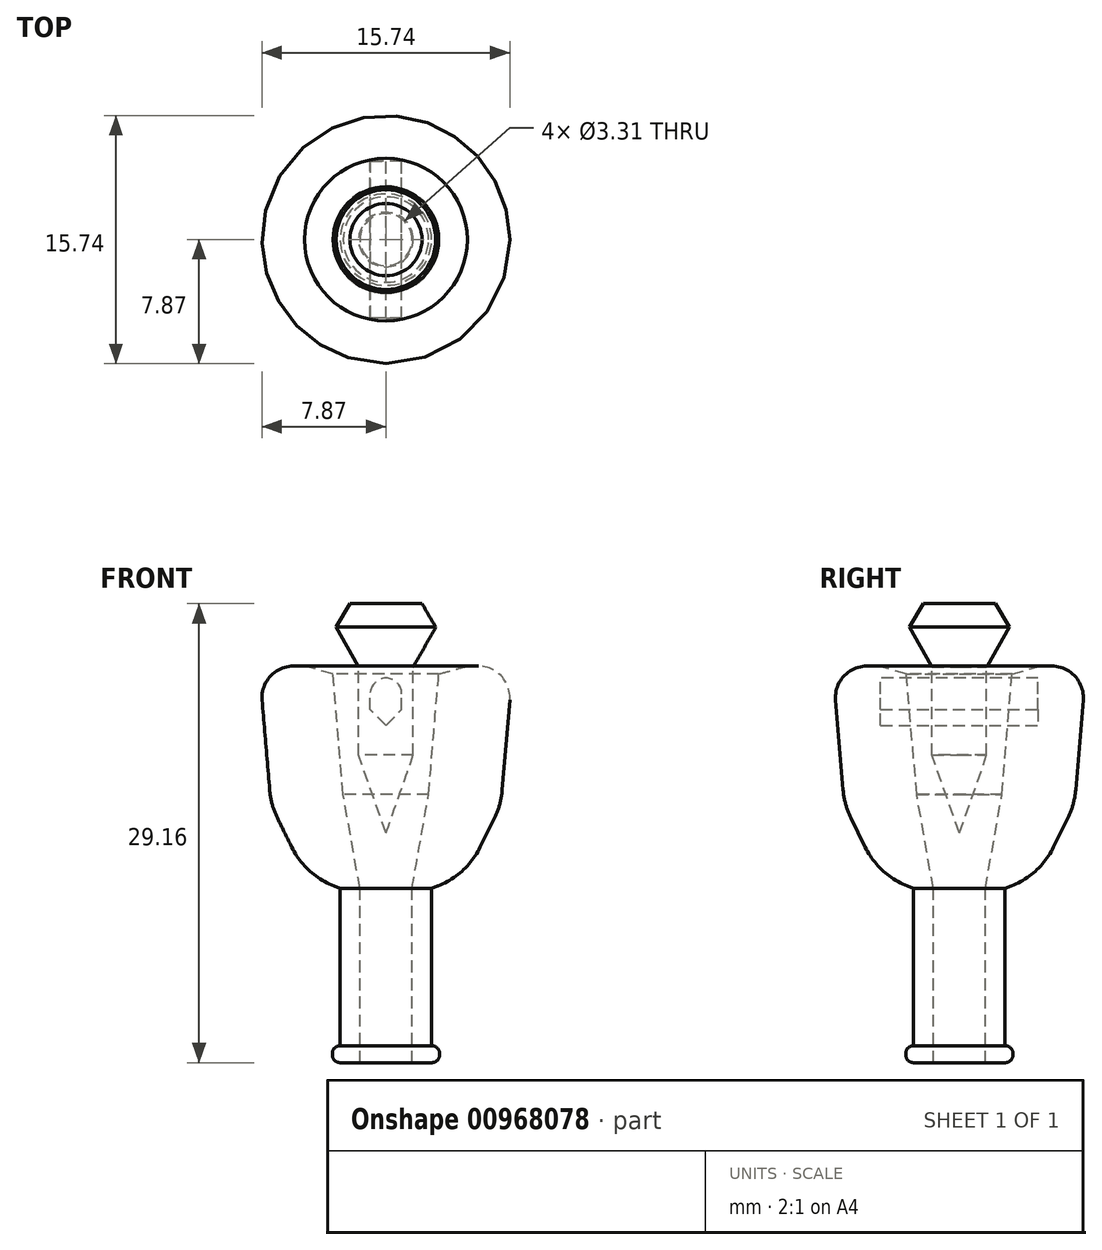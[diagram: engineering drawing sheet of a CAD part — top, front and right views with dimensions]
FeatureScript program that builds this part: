
annotation { "Feature Type Name" : "Feature", "Feature Type Description" : "" }
export const myFeature = defineFeature(function(context is Context, id is Id, definition is map)
    precondition{}
    {
        {
            var Q0;
            Q0=qCreatedBy(makeId("Front.planeOp"),FACE);
            var sketch = newSketch(context, id + "F0", { "sketchPlane" : qUnion([Q0])});
            skLineSegment(sketch, "E0", {"start": v(0, 29.16) * mm, "end": v(-4, 29.16) * mm});
            skLineSegment(sketch, "E1", {"start": v(-4, 29.16) * mm, "end": v(-1.73, 25.13) * mm});
            skLineSegment(sketch, "E2", {"start": v(-1.73, 25.13) * mm, "end": v(-1.73, 22.74) * mm});
            skLineSegment(sketch, "E3", {"start": v(-1.73, 22.74) * mm, "end": v(-1.73, 19.53) * mm});
            skLineSegment(sketch, "E4", {"start": v(-5.17, 25.2) * mm, "end": v(-8.05, 25.2) * mm});
            skLineSegment(sketch, "E5", {"start": v(-8.05, 25.2) * mm, "end": v(-7.3, 16.38) * mm});
            skLineSegment(sketch, "E6", {"start": v(-7.3, 16.38) * mm, "end": v(-5.13, 11.94) * mm});
            skLineSegment(sketch, "E7", {"start": v(-5.13, 11.94) * mm, "end": v(-2.9, 11.08) * mm});
            skLineSegment(sketch, "E8", {"start": v(-3, 0) * mm, "end": v(-1.66, 0) * mm});
            skLineSegment(sketch, "E9", {"start": v(-1.66, 0) * mm, "end": v(-1.66, 11.07) * mm});
            skLineSegment(sketch, "E10", {"start": v(0, 29.16) * mm, "end": v(0, 0) * mm, "construction": true});
            skLineSegment(sketch, "E11", {"start": v(-1.73, 19.53) * mm, "end": v(0, 14.58) * mm});
            skLineSegment(sketch, "E12", {"start": v(-5.17, 25.2) * mm, "end": v(-3.35, 24.68) * mm});
            skLineSegment(sketch, "E13", {"start": v(-3.35, 24.68) * mm, "end": v(-2.71, 17.04) * mm});
            skLineSegment(sketch, "E14", {"start": v(-2.71, 17.04) * mm, "end": v(-1.66, 11.07) * mm});
            skLineSegment(sketch, "E15", {"start": v(-2.9, 11.08) * mm, "end": v(-2.9, 1.08) * mm});
            skLineSegment(sketch, "E16", {"start": v(-2.9, 1.08) * mm, "end": v(-3.4, 1.08) * mm});
            skLineSegment(sketch, "E17", {"start": v(-3.4, 1.08) * mm, "end": v(-3.4, 0) * mm});
            skLineSegment(sketch, "E18", {"start": v(-3.4, 0) * mm, "end": v(-3, 0) * mm});
            skLineSegment(sketch, "E19", {"start": v(0, 29.16) * mm, "end": v(0, 14.58) * mm});
            skSolve(sketch);
        }
        {
            var Q0;
            Q0=makeQuery(id+"F0.imprint","IMPRINT",FACE,{"disambiguationData":[TD([[makeQuery(id+"F0.imprint","IMPRINT",EDGE,{"derivedFrom":sQuery(id+"F0.wireOp",EDGE,"E0")}),1.0]])]});
            var Q1;
            Q1=makeQuery(id+"F0.imprint","IMPRINT",FACE,{"disambiguationData":[TD([[makeQuery(id+"F0.imprint","IMPRINT",EDGE,{"derivedFrom":sQuery(id+"F0.wireOp",EDGE,"E4")}),1.0]])]});
            var Q2;
            Q2=sQuery(id+"F0.wireOp",EDGE,"E10");
            revolve(context, id + "F1", {"surfaceOperationType" : NewSurfaceOperationType.NEW, "entities" : qUnion([Q0, Q1]), "axis" : qUnion([Q2]), "revolveType" : RevolveType.FULL});
        }
        {
            var Q0;
            Q0=qCreatedBy(makeId("Front.planeOp"),FACE);
            var sketch = newSketch(context, id + "F2", { "sketchPlane" : qUnion([Q0])});
            skLineSegment(sketch, "E20.bottom", {"start": v(1, 21.42) * mm, "end": v(-1, 21.42) * mm});
            skLineSegment(sketch, "E20.top", {"start": v(1, 24.42) * mm, "end": v(-1, 24.42) * mm});
            skLineSegment(sketch, "E20.left", {"start": v(1, 21.42) * mm, "end": v(1, 24.42) * mm});
            skLineSegment(sketch, "E20.right", {"start": v(-1, 21.42) * mm, "end": v(-1, 24.42) * mm});
            skPoint(sketch, "E20.middle", {"position": v(0, 22.92) * mm});
            skSolve(sketch);
        }
        {
            var Q0;
            Q0=makeQuery(id+"F2.imprint","IMPRINT",FACE,{"disambiguationData":[TD([[makeQuery(id+"F2.imprint","IMPRINT",EDGE,{"derivedFrom":sQuery(id+"F2.wireOp",EDGE,"E20.bottom")}),-1.0]])]});
            extrude(context, id + "F3", {"entities" : qUnion([Q0]), "endBound" : BoundingType.SYMMETRIC, "depth" : 10 * mm, "offsetDistance" : 25 * mm});
        }
        {
            var Q0;
            Q0=makeQuery(id+"F3.opExtrude","SWEPT_EDGE",EDGE,{"disambiguationData":[OSD([sQuery(id+"F2.wireOp",EDGE,"E20.bottom"),sQuery(id+"F2.wireOp",EDGE,"E20.right")])]});
            var Q1;
            Q1=makeQuery(id+"F3.opExtrude","SWEPT_EDGE",EDGE,{"disambiguationData":[OSD([sQuery(id+"F2.wireOp",EDGE,"E20.bottom"),sQuery(id+"F2.wireOp",EDGE,"E20.left")])]});
            chamfer(context, id + "F4", {"entities" : qUnion([Q0, Q1]), "width" : 1 * mm, "tangentPropagation" : true});
        }
        {
            var Q0;
            Q0=makeQuery(id+"F3.opExtrude","SWEPT_EDGE",EDGE,{"disambiguationData":[OSD([sQuery(id+"F2.wireOp",EDGE,"E20.top"),sQuery(id+"F2.wireOp",EDGE,"E20.right")])]});
            var Q1;
            Q1=makeQuery(id+"F3.opExtrude","SWEPT_EDGE",EDGE,{"disambiguationData":[OSD([sQuery(id+"F2.wireOp",EDGE,"E20.top"),sQuery(id+"F2.wireOp",EDGE,"E20.left")])]});
            fillet(context, id + "F5", {"entities" : qUnion([Q0, Q1]), "radius" : 1 * mm, "tangentPropagation" : true, "allowEdgeOverflow" : false});
        }
        {
            var Q0;
            Q0=makeQuery(id+"F1.opRevolve","SWEPT_EDGE",EDGE,{"disambiguationData":[OSD([sQuery(id+"F0.wireOp",EDGE,"E4"),sQuery(id+"F0.wireOp",EDGE,"E5")])]});
            fillet(context, id + "F6", {"entities" : qUnion([Q0]), "radius" : 2 * mm, "tangentPropagation" : true, "allowEdgeOverflow" : false});
        }
        {
            var Q0;
            Q0=makeQuery(id+"F1.opRevolve","SWEPT_EDGE",EDGE,{"disambiguationData":[OSD([sQuery(id+"F0.wireOp",EDGE,"E0"),sQuery(id+"F0.wireOp",EDGE,"E1")])]});
            chamfer(context, id + "F7", {"entities" : qUnion([Q0]), "width" : 1 * mm, "tangentPropagation" : true});
        }
        {
            var Q0;
            Q0=makeQuery(id+"F1.opRevolve","SWEPT_EDGE",EDGE,{"disambiguationData":[OSD([sQuery(id+"F0.wireOp",EDGE,"E5"),sQuery(id+"F0.wireOp",EDGE,"E6")])]});
            var Q1;
            Q1=makeQuery(id+"F1.opRevolve","SWEPT_EDGE",EDGE,{"disambiguationData":[OSD([sQuery(id+"F0.wireOp",EDGE,"E6"),sQuery(id+"F0.wireOp",EDGE,"E7")])]});
            fillet(context, id + "F8", {"entities" : qUnion([Q0, Q1]), "radius" : 5 * mm, "tangentPropagation" : true, "allowEdgeOverflow" : false});
        }
        {
            var Q0;
            Q0=makeQuery(id+"F1.opRevolve","SWEPT_EDGE",EDGE,{"disambiguationData":[OSD([sQuery(id+"F0.wireOp",EDGE,"E17"),sQuery(id+"F0.wireOp",EDGE,"E18")])]});
            var Q1;
            Q1=makeQuery(id+"F1.opRevolve","SWEPT_EDGE",EDGE,{"disambiguationData":[OSD([sQuery(id+"F0.wireOp",EDGE,"E16"),sQuery(id+"F0.wireOp",EDGE,"E17")])]});
            fillet(context, id + "F9", {"entities" : qUnion([Q0, Q1]), "radius" : .5 * mm, "tangentPropagation" : true, "allowEdgeOverflow" : false});
        }
    });
